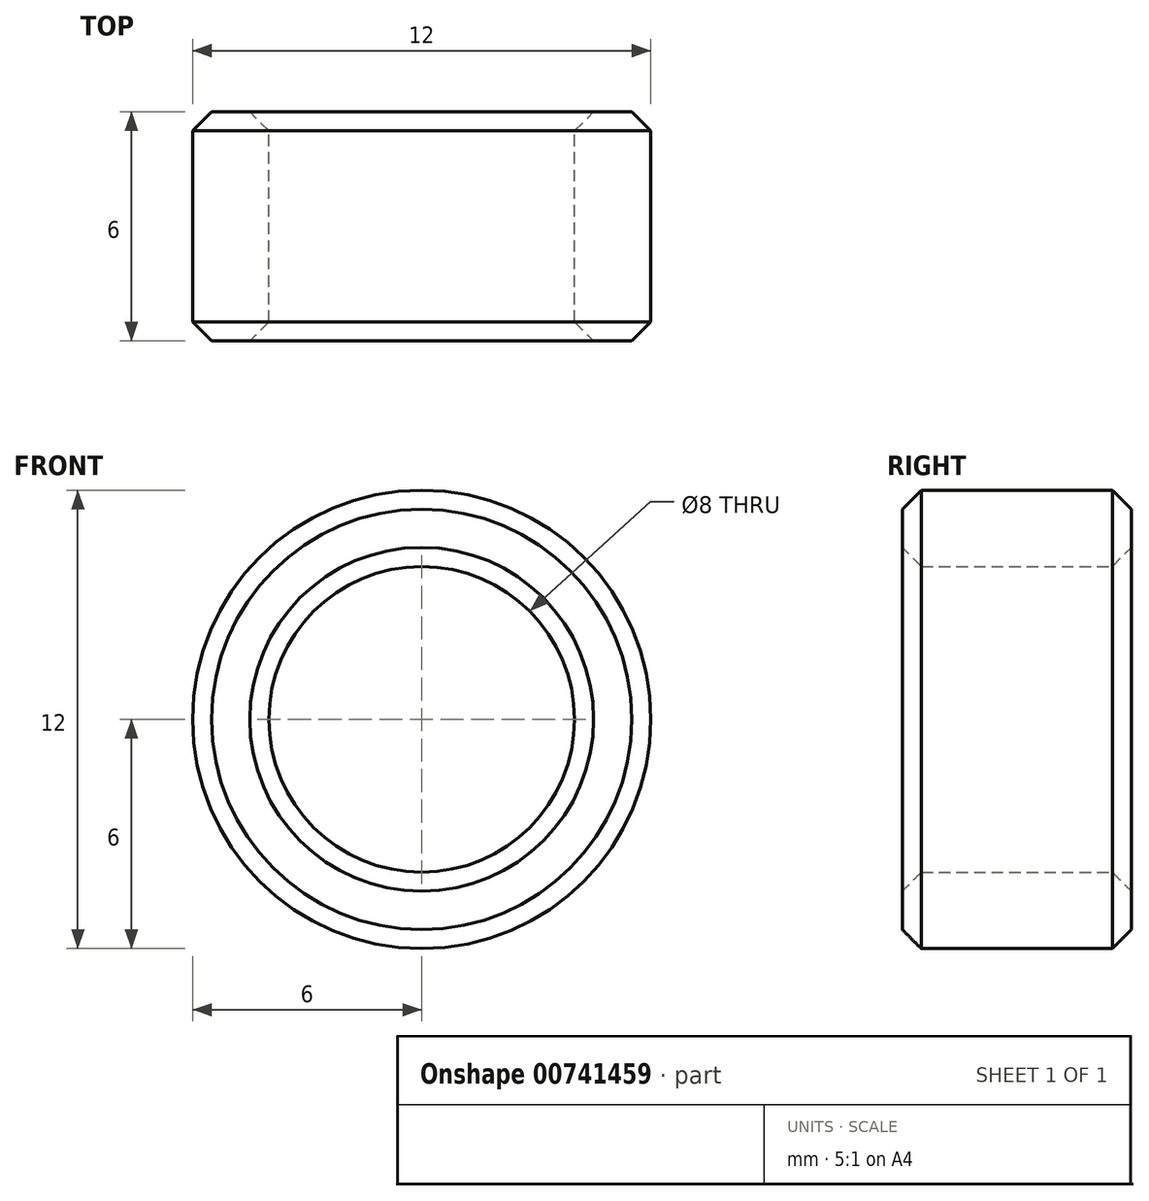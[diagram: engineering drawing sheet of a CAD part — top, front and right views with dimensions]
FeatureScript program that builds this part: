
annotation { "Feature Type Name" : "Feature", "Feature Type Description" : "" }
export const myFeature = defineFeature(function(context is Context, id is Id, definition is map)
    precondition{}
    {
        {
            var Q0;
            Q0=qCreatedBy(makeId("Front.planeOp"),FACE);
            var sketch = newSketch(context, id + "F0", { "sketchPlane" : qUnion([Q0])});
            skCircle(sketch, "E0", {"center": v(0, 0) * mm, "radius": 6 * mm});
            skCircle(sketch, "E1", {"center": v(0, 0) * mm, "radius": 4 * mm});
            skSolve(sketch);
        }
        {
            var Q0;
            Q0 = qSketchRegion(id + "F0", true);
            extrude(context, id + "F1", {"entities" : qUnion([Q0]), "depth" : 6 * mm, "offsetDistance" : 25 * mm});
        }
        {
            var Q0;
            Q0=makeQuery(id+"F1.opExtrude","CAP_EDGE",EDGE,{"disambiguationData":[OSD([sQuery(id+"F0.wireOp",EDGE,"E1")])],"isStart":true});
            var Q1;
            Q1=makeQuery(id+"F1.opExtrude","CAP_EDGE",EDGE,{"disambiguationData":[OSD([sQuery(id+"F0.wireOp",EDGE,"E0")])],"isStart":true});
            var Q2;
            Q2=makeQuery(id+"F1.opExtrude","CAP_EDGE",EDGE,{"disambiguationData":[OSD([sQuery(id+"F0.wireOp",EDGE,"E1")])],"isStart":false});
            var Q3;
            Q3=makeQuery(id+"F1.opExtrude","SWEPT_FACE",FACE,{"disambiguationData":[OSD([sQuery(id+"F0.wireOp",EDGE,"E0")])]});
            chamfer(context, id + "F2", {"entities" : qUnion([Q0, Q1, Q2, Q3]), "width" : .5 * mm, "tangentPropagation" : true});
        }
    });
